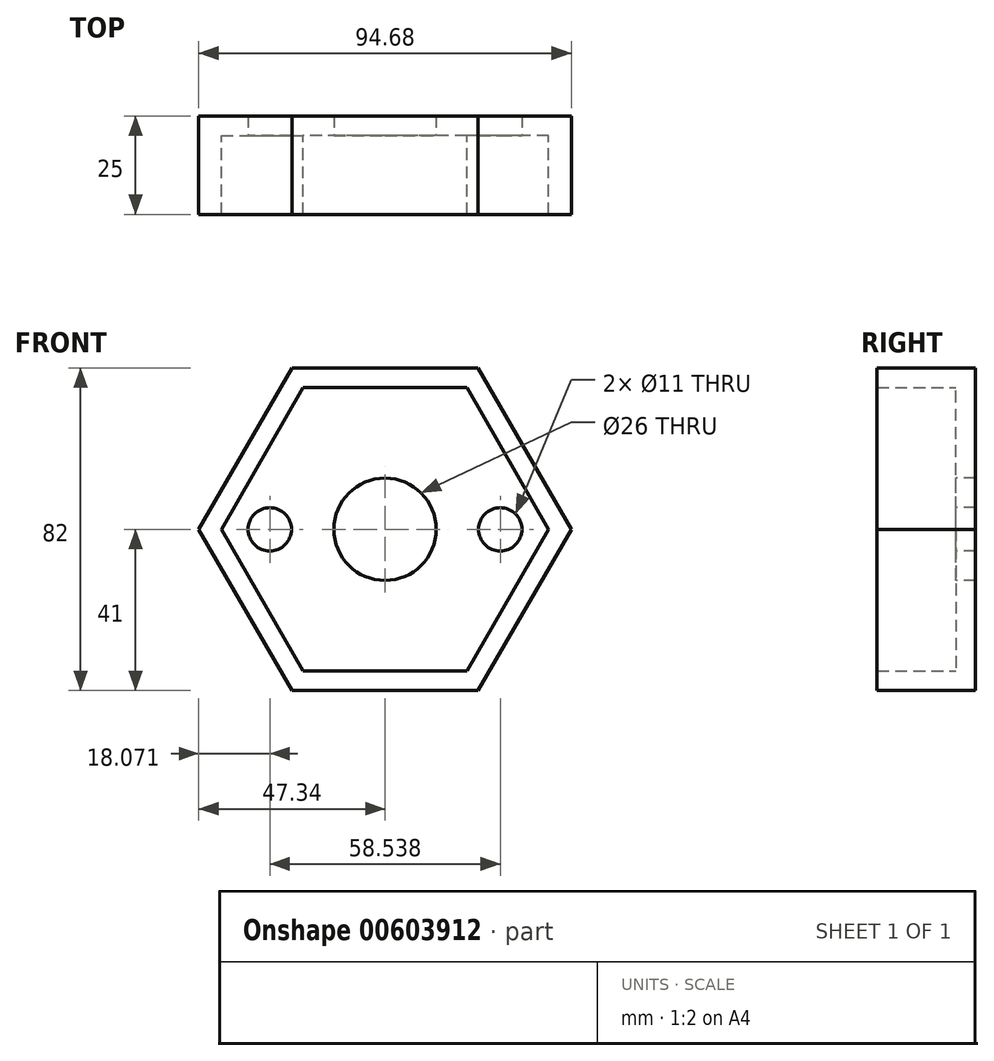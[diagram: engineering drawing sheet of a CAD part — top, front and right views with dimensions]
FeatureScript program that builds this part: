
annotation { "Feature Type Name" : "Feature", "Feature Type Description" : "" }
export const myFeature = defineFeature(function(context is Context, id is Id, definition is map)
    precondition{}
    {
        {
            var Q0;
            Q0=qCreatedBy(makeId("Front.planeOp"),FACE);
            var sketch = newSketch(context, id + "F0", { "sketchPlane" : qUnion([Q0])});
            skLineSegment(sketch, "E0.0", {"start": v(41.57, 0) * mm, "end": v(20.78, -36) * mm});
            skLineSegment(sketch, "E0.1", {"start": v(20.78, -36) * mm, "end": v(-20.78, -36) * mm});
            skLineSegment(sketch, "E0.3", {"start": v(-41.57, 0) * mm, "end": v(-20.78, 36) * mm});
            skLineSegment(sketch, "E0.4", {"start": v(-20.78, 36) * mm, "end": v(20.78, 36) * mm});
            skLineSegment(sketch, "E1.0", {"start": v(47.34, 0) * mm, "end": v(23.67, -41) * mm});
            skLineSegment(sketch, "E1.1", {"start": v(23.67, -41) * mm, "end": v(-23.67, -41) * mm});
            skLineSegment(sketch, "E1.2", {"start": v(-23.67, -41) * mm, "end": v(-47.34, 0) * mm});
            skLineSegment(sketch, "E1.3", {"start": v(-47.34, 0) * mm, "end": v(-23.67, 41) * mm});
            skLineSegment(sketch, "E1.4", {"start": v(-23.67, 41) * mm, "end": v(23.67, 41) * mm});
            skLineSegment(sketch, "E2", {"start": v(-41.57, 0) * mm, "end": v(-20.78, -36) * mm});
            skLineSegment(sketch, "E3", {"start": v(20.78, 36) * mm, "end": v(41.57, 0) * mm});
            skLineSegment(sketch, "E4", {"start": v(23.67, 41) * mm, "end": v(47.34, 0) * mm});
            skSolve(sketch);
        }
        {
            var Q0;
            Q0=makeQuery(id+"F0.imprint","IMPRINT",FACE,{"disambiguationData":[TD([[makeQuery(id+"F0.imprint","IMPRINT",EDGE,{"derivedFrom":sQuery(id+"F0.wireOp",EDGE,"E0.0")}),-1.0]])]});
            var Q1;
            Q1=makeQuery(id+"F0.imprint","IMPRINT",FACE,{"disambiguationData":[TD([[makeQuery(id+"F0.imprint","IMPRINT",EDGE,{"derivedFrom":sQuery(id+"F0.wireOp",EDGE,"E0.0")}),1.0]])]});
            var Q2;
            Q2 = qSketchRegion(id + "F0", true);
            extrude(context, id + "F1", {"entities" : qUnion([Q0, Q1, Q2]), "oppositeDirection" : true, "depth" : 5 * mm, "offsetDistance" : 25 * mm});
        }
        {
            var Q0;
            Q0 = qSketchRegion(id + "F0", true);
            extrude(context, id + "F2", {"entities" : qUnion([Q0]), "operationType" : NewBodyOperationType.ADD, "depth" : 20 * mm, "offsetDistance" : 25 * mm});
        }
        {
            var Q0;
            Q0=makeQuery(id+"F1.opExtrude","CAP_FACE",FACE,{"disambiguationData":[OSD([sQuery(id+"F0.wireOp",EDGE,"E1.0"),sQuery(id+"F0.wireOp",EDGE,"E1.1"),sQuery(id+"F0.wireOp",EDGE,"E1.2"),sQuery(id+"F0.wireOp",EDGE,"E1.3"),sQuery(id+"F0.wireOp",EDGE,"E1.4"),sQuery(id+"F0.wireOp",EDGE,"E1.5")])],"isStart":true});
            var sketch = newSketch(context, id + "F3", { "sketchPlane" : qUnion([Q0])});
            skCircle(sketch, "E5", {"center": v(0, 0) * mm, "radius": 13 * mm});
            skSolve(sketch);
        }
        {
            var Q0;
            Q0=makeQuery(id+"F3.imprint","IMPRINT",FACE,{"disambiguationData":[TD([[makeQuery(id+"F3.imprint","IMPRINT",EDGE,{"derivedFrom":sQuery(id+"F3.wireOp",EDGE,"E5")}),1.0]])]});
            extrude(context, id + "F4", {"entities" : qUnion([Q0]), "operationType" : NewBodyOperationType.REMOVE, "oppositeDirection" : true, "depth" : 25 * mm, "offsetDistance" : 25 * mm});
        }
        {
            var Q0;
            Q0=makeQuery(id+"F1.opExtrude","CAP_FACE",FACE,{"disambiguationData":[OSD([sQuery(id+"F0.wireOp",EDGE,"E1.0"),sQuery(id+"F0.wireOp",EDGE,"E1.1"),sQuery(id+"F0.wireOp",EDGE,"E1.2"),sQuery(id+"F0.wireOp",EDGE,"E1.3"),sQuery(id+"F0.wireOp",EDGE,"E1.4"),sQuery(id+"F0.wireOp",EDGE,"E1.5")])],"isStart":true});
            var sketch = newSketch(context, id + "F5", { "sketchPlane" : qUnion([Q0])});
            skCircle(sketch, "E6", {"center": v(-29.27, 0) * mm, "radius": 5.5 * mm});
            skCircle(sketch, "E7", {"center": v(29.27, 0) * mm, "radius": 5.5 * mm});
            skSolve(sketch);
        }
        {
            var Q0;
            Q0=makeQuery(id+"F5.imprint","IMPRINT",FACE,{"disambiguationData":[TD([[makeQuery(id+"F5.imprint","IMPRINT",EDGE,{"derivedFrom":sQuery(id+"F5.wireOp",EDGE,"E7")}),1.0]])]});
            var Q1;
            Q1=makeQuery(id+"F5.imprint","IMPRINT",FACE,{"disambiguationData":[TD([[makeQuery(id+"F5.imprint","IMPRINT",EDGE,{"derivedFrom":sQuery(id+"F5.wireOp",EDGE,"E6")}),1.0]])]});
            extrude(context, id + "F6", {"entities" : qUnion([Q0, Q1]), "operationType" : NewBodyOperationType.REMOVE, "oppositeDirection" : true, "depth" : 25 * mm, "offsetDistance" : 25 * mm});
        }
    });
